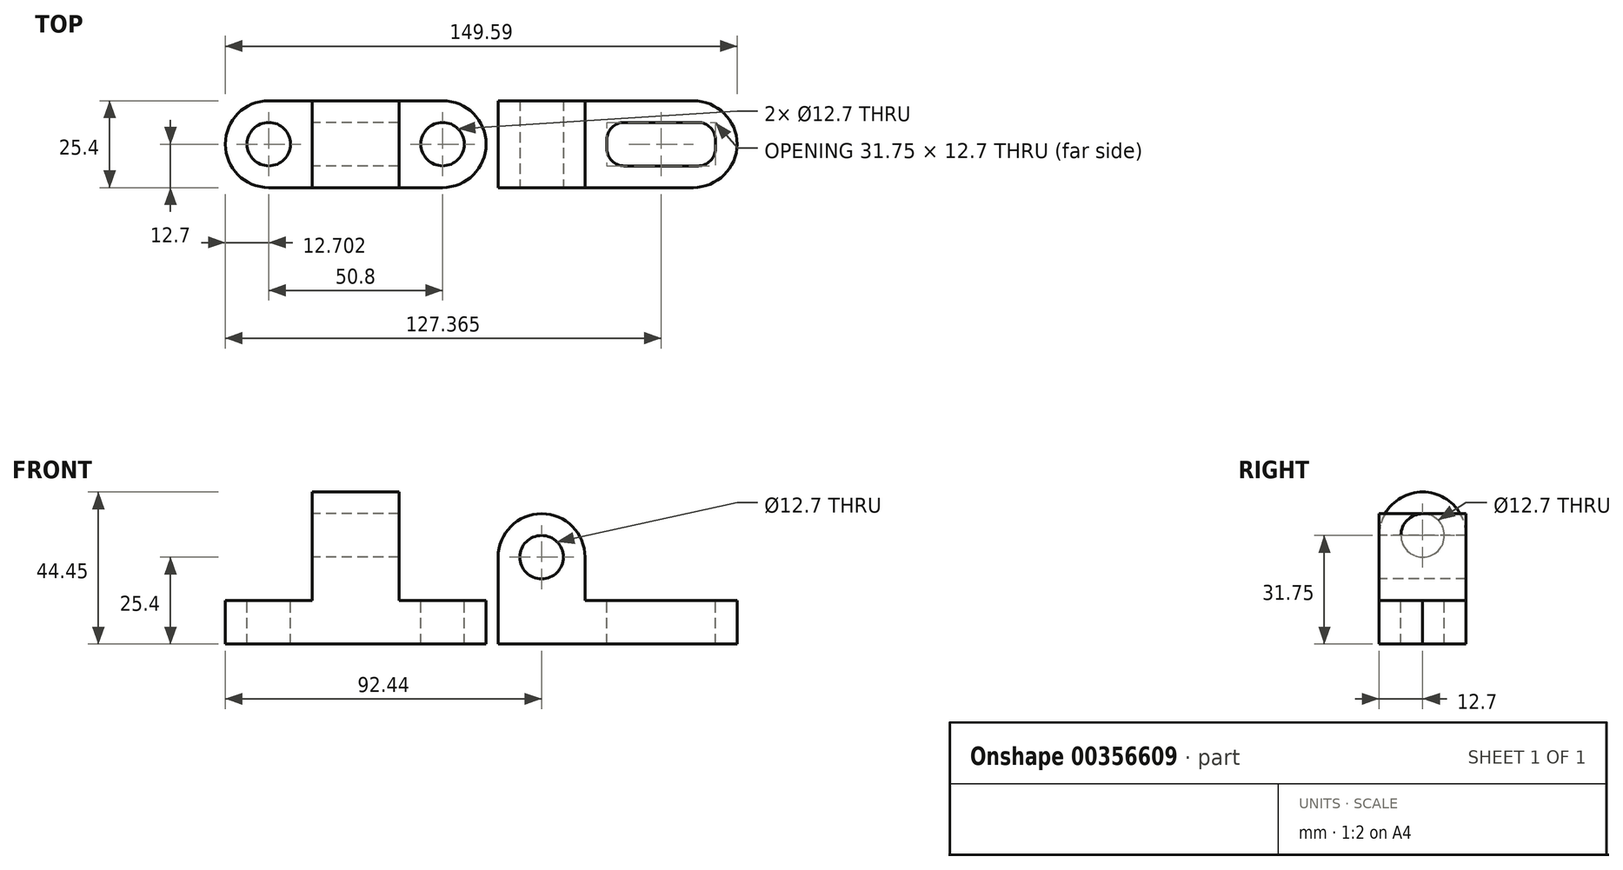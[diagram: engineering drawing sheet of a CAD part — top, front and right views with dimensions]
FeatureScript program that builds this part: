
annotation { "Feature Type Name" : "Feature", "Feature Type Description" : "" }
export const myFeature = defineFeature(function(context is Context, id is Id, definition is map)
    precondition{}
    {
        {
            var Q0;
            Q0=qCreatedBy(makeId("Top.planeOp"),FACE);
            var sketch = newSketch(context, id + "F0", { "sketchPlane" : qUnion([Q0])});
            skLineSegment(sketch, "E0.bottom", {"start": v(0, 0) * mm, "end": v(69.85, 0) * mm});
            skLineSegment(sketch, "E0.top", {"start": v(0, 25.4) * mm, "end": v(69.85, 25.4) * mm});
            skLineSegment(sketch, "E0.left", {"start": v(0, 0) * mm, "end": v(0, 25.4) * mm});
            skLineSegment(sketch, "E0.right", {"start": v(69.85, 0) * mm, "end": v(69.85, 25.4) * mm});
            skSolve(sketch);
        }
        {
            var Q0;
            Q0 = qSketchRegion(id + "F0", true);
            extrude(context, id + "F1", {"entities" : qUnion([Q0]), "depth" : 12.7 * mm});
        }
        {
            var Q0;
            Q0=makeQuery(id+"F1.opExtrude","CAP_FACE",FACE,{"disambiguationData":[OSD([sQuery(id+"F0.wireOp",EDGE,"E0.bottom"),sQuery(id+"F0.wireOp",EDGE,"E0.top"),sQuery(id+"F0.wireOp",EDGE,"E0.left"),sQuery(id+"F0.wireOp",EDGE,"E0.right")])],"isStart":false});
            var sketch = newSketch(context, id + "F2", { "sketchPlane" : qUnion([Q0])});
            skLineSegment(sketch, "E1", {"start": v(25.4, 25.4) * mm, "end": v(25.4, 0) * mm});
            skSolve(sketch);
        }
        {
            var Q0;
            {var subQ0=sQuery(id+"F2.wireOp",EDGE,"E1");Q0=makeQuery(id+"F2.imprint","IMPRINT",FACE,{"disambiguationData":[TD([[makeQuery(id+"F2.imprint","IMPRINT",EDGE,{"derivedFrom":subQ0}),-1.0]])]});}
            extrude(context, id + "F3", {"entities" : qUnion([Q0]), "operationType" : NewBodyOperationType.ADD, "depth" : 25.4 * mm});
        }
        {
            var Q0;
            {var subQ0=sQuery(id+"F0.wireOp",EDGE,"E0.bottom");Q0=makeQuery(id+"F3.boolean.opBoolean","MERGE",FACE,{"derivedFrom":[makeQuery(id+"F1.opExtrude","SWEPT_FACE",FACE,{"disambiguationData":[OSD([subQ0])]}),makeQuery(id+"F3.opExtrude","SWEPT_FACE",FACE,{"disambiguationData":[OSD([subQ0])]})]});}
            var sketch = newSketch(context, id + "F4", { "sketchPlane" : qUnion([Q0])});
            skCircle(sketch, "E2", {"center": v(12.7, 25.4) * mm, "radius": 6.35 * mm});
            skPoint(sketch, "E2.centerSnap0", {"position": v(25.4, 25.4) * mm});
            skPoint(sketch, "E2.centerSnap1", {"position": v(12.7, 38.1) * mm});
            skSolve(sketch);
        }
        {
            var Q0;
            Q0=sQuery(id+"F4.wireOp",VERTEX,"E2.center");
            var Q1;
            Q1=makeQuery(id+"F1.opExtrude","SWEPT_BODY",BODY,{"disambiguationData":[OSD([sQuery(id+"F0.wireOp",EDGE,"E0.bottom"),sQuery(id+"F0.wireOp",EDGE,"E0.top"),sQuery(id+"F0.wireOp",EDGE,"E0.left"),sQuery(id+"F0.wireOp",EDGE,"E0.right")])]});
            hole(context, id + "F5", {"style" : HoleStyle.SIMPLE, "endStyle" : HoleEndStyle.THROUGH, "holeDiameter" : 12.7 * mm, "isTappedThrough" : true, "tappedDepth" : 12.7 * mm, "tapClearance" : 3, "locations" : qUnion([Q0]), "scope" : qUnion([Q1])});
        }
        {
            var Q0;
            Q0=makeQuery(id+"F1.opExtrude","CAP_FACE",FACE,{"disambiguationData":[OSD([sQuery(id+"F0.wireOp",EDGE,"E0.bottom"),sQuery(id+"F0.wireOp",EDGE,"E0.top"),sQuery(id+"F0.wireOp",EDGE,"E0.left"),sQuery(id+"F0.wireOp",EDGE,"E0.right")])],"isStart":false});
            var sketch = newSketch(context, id + "F6", { "sketchPlane" : qUnion([Q0])});
            skLineSegment(sketch, "E3.bottom", {"start": v(31.75, 19.05) * mm, "end": v(63.5, 19.05) * mm});
            skLineSegment(sketch, "E3.top", {"start": v(31.75, 6.35) * mm, "end": v(63.5, 6.35) * mm});
            skLineSegment(sketch, "E3.left", {"start": v(31.75, 19.05) * mm, "end": v(31.75, 6.35) * mm});
            skLineSegment(sketch, "E3.right", {"start": v(63.5, 19.05) * mm, "end": v(63.5, 6.35) * mm});
            skSolve(sketch);
        }
        {
            var Q0;
            Q0 = qSketchRegion(id + "F6", true);
            extrude(context, id + "F7", {"entities" : qUnion([Q0]), "operationType" : NewBodyOperationType.REMOVE, "oppositeDirection" : true, "depth" : 12.7 * mm});
        }
        {
            var Q0;
            {var subQ0=sQuery(id+"F0.wireOp",EDGE,"E0.bottom");Q0=makeQuery(id+"F3.boolean.opBoolean","MERGE",FACE,{"derivedFrom":[makeQuery(id+"F1.opExtrude","SWEPT_FACE",FACE,{"disambiguationData":[OSD([subQ0])]}),makeQuery(id+"F3.opExtrude","SWEPT_FACE",FACE,{"disambiguationData":[OSD([subQ0])]})]});}
            var sketch = newSketch(context, id + "F8", { "sketchPlane" : qUnion([Q0])});
            skCircle(sketch, "E4", {"center": v(12.7, 25.4) * mm, "radius": 12.7 * mm});
            skPoint(sketch, "E4.first.point", {"position": v(12.7, 38.1) * mm});
            skPoint(sketch, "E4.second.point", {"position": v(25.4, 25.4) * mm});
            skPoint(sketch, "E4.third.point", {"position": v(0, 25.4) * mm});
            skPoint(sketch, "E4.third.point.positionSnap0", {"position": v(25.4, 25.4) * mm});
            skSolve(sketch);
        }
        {
            var Q0;
            {var subQ0=sQuery(id+"F8.wireOp",EDGE,"E4");var subQ1=sQuery(id+"F0.wireOp",EDGE,"E0.bottom");var subQ2=makeQuery(id+"F3.opExtrude","CAP_EDGE",EDGE,{"disambiguationData":[OSD([subQ1])],"isStart":false});var subQ3=makeQuery(id+"F8.imprint","INTERSECT",VERTEX,{"derivedFrom":[subQ2,subQ0]});Q0=makeQuery(id+"F8.imprint","IMPRINT",FACE,{"disambiguationData":[TD([[makeQuery(id+"F8.imprint","IMPRINT",EDGE,{"disambiguationData":[TD([[subQ3,-1.0]])],"derivedFrom":subQ0}),-1.0]])]});}
            extrude(context, id + "F9", {"entities" : qUnion([Q0]), "operationType" : NewBodyOperationType.REMOVE, "oppositeDirection" : true, "depth" : 25.4 * mm});
        }
        {
            var Q0;
            {var subQ0=sQuery(id+"F8.wireOp",EDGE,"E4");var subQ1=sQuery(id+"F0.wireOp",EDGE,"E0.bottom");var subQ2=makeQuery(id+"F3.opExtrude","CAP_EDGE",EDGE,{"disambiguationData":[OSD([subQ1])],"isStart":false});var subQ3=makeQuery(id+"F8.imprint","INTERSECT",VERTEX,{"derivedFrom":[subQ2,subQ0]});Q0=makeQuery(id+"F8.imprint","IMPRINT",FACE,{"disambiguationData":[TD([[makeQuery(id+"F8.imprint","IMPRINT",EDGE,{"disambiguationData":[TD([[subQ3,1.0]])],"derivedFrom":subQ0}),-1.0]])]});}
            extrude(context, id + "F10", {"entities" : qUnion([Q0]), "operationType" : NewBodyOperationType.REMOVE, "oppositeDirection" : true, "depth" : 25.4 * mm});
        }
        {
            var Q0;
            Q0=makeQuery(id+"F7.boolean.opBoolean","COPY",EDGE,{"derivedFrom":makeQuery(id+"F7.opExtrude","SWEPT_EDGE",EDGE,{"disambiguationData":[OSD([sQuery(id+"F6.wireOp",EDGE,"E3.bottom"),sQuery(id+"F6.wireOp",EDGE,"E3.left")])]})});
            var Q1;
            Q1=makeQuery(id+"F7.boolean.opBoolean","COPY",EDGE,{"derivedFrom":makeQuery(id+"F7.opExtrude","SWEPT_EDGE",EDGE,{"disambiguationData":[OSD([sQuery(id+"F6.wireOp",EDGE,"E3.top"),sQuery(id+"F6.wireOp",EDGE,"E3.left")])]})});
            var Q2;
            Q2=makeQuery(id+"F7.boolean.opBoolean","COPY",EDGE,{"derivedFrom":makeQuery(id+"F7.opExtrude","SWEPT_EDGE",EDGE,{"disambiguationData":[OSD([sQuery(id+"F6.wireOp",EDGE,"E3.bottom"),sQuery(id+"F6.wireOp",EDGE,"E3.right")])]})});
            var Q3;
            Q3=makeQuery(id+"F7.boolean.opBoolean","COPY",EDGE,{"derivedFrom":makeQuery(id+"F7.opExtrude","SWEPT_EDGE",EDGE,{"disambiguationData":[OSD([sQuery(id+"F6.wireOp",EDGE,"E3.top"),sQuery(id+"F6.wireOp",EDGE,"E3.right")])]})});
            fillet(context, id + "F11", {"entities" : qUnion([Q0, Q1, Q2, Q3]), "radius" : 5.08 * mm, "tangentPropagation" : true, "allowEdgeOverflow" : false});
        }
        {
            var Q0;
            Q0=makeQuery(id+"F1.opExtrude","SWEPT_EDGE",EDGE,{"disambiguationData":[OSD([sQuery(id+"F0.wireOp",EDGE,"E0.top"),sQuery(id+"F0.wireOp",EDGE,"E0.right")])]});
            var Q1;
            Q1=makeQuery(id+"F1.opExtrude","SWEPT_EDGE",EDGE,{"disambiguationData":[OSD([sQuery(id+"F0.wireOp",EDGE,"E0.bottom"),sQuery(id+"F0.wireOp",EDGE,"E0.right")])]});
            fillet(context, id + "F12", {"entities" : qUnion([Q0, Q1]), "radius" : 12.88 * mm, "tangentPropagation" : true, "allowEdgeOverflow" : false});
        }
        {
            var Q0;
            Q0=qCreatedBy(makeId("Top.planeOp"),FACE);
            var sketch = newSketch(context, id + "F13", { "sketchPlane" : qUnion([Q0])});
            skLineSegment(sketch, "E5.bottom", {"start": v(-79.74, 0) * mm, "end": v(-3.54, 0) * mm});
            skLineSegment(sketch, "E5.top", {"start": v(-79.74, 25.4) * mm, "end": v(-3.54, 25.4) * mm});
            skLineSegment(sketch, "E5.left", {"start": v(-79.74, 0) * mm, "end": v(-79.74, 25.4) * mm});
            skLineSegment(sketch, "E5.right", {"start": v(-3.54, 0) * mm, "end": v(-3.54, 25.4) * mm});
            skSolve(sketch);
        }
        {
            var Q0;
            Q0 = qSketchRegion(id + "F13", true);
            extrude(context, id + "F14", {"entities" : qUnion([Q0]), "depth" : 12.7 * mm});
        }
        {
            var Q0;
            Q0=makeQuery(id+"F14.opExtrude","CAP_FACE",FACE,{"disambiguationData":[OSD([sQuery(id+"F13.wireOp",EDGE,"E5.bottom"),sQuery(id+"F13.wireOp",EDGE,"E5.top"),sQuery(id+"F13.wireOp",EDGE,"E5.left"),sQuery(id+"F13.wireOp",EDGE,"E5.right")])],"isStart":false});
            var sketch = newSketch(context, id + "F15", { "sketchPlane" : qUnion([Q0])});
            skLineSegment(sketch, "E6.bottom", {"start": v(-54.34, 25.4) * mm, "end": v(-28.94, 25.4) * mm});
            skLineSegment(sketch, "E6.top", {"start": v(-54.34, 0) * mm, "end": v(-28.94, 0) * mm});
            skLineSegment(sketch, "E6.left", {"start": v(-54.34, 25.4) * mm, "end": v(-54.34, 0) * mm});
            skLineSegment(sketch, "E6.right", {"start": v(-28.94, 25.4) * mm, "end": v(-28.94, 0) * mm});
            skSolve(sketch);
        }
        {
            var Q0;
            Q0=makeQuery(id+"F15.imprint","IMPRINT",FACE,{"disambiguationData":[TD([[makeQuery(id+"F15.imprint","IMPRINT",EDGE,{"derivedFrom":sQuery(id+"F15.wireOp",EDGE,"E6.bottom")}),-1.0]])]});
            extrude(context, id + "F16", {"entities" : qUnion([Q0]), "operationType" : NewBodyOperationType.ADD, "depth" : 31.75 * mm});
        }
        {
            var Q0;
            {var subQ0=sQuery(id+"F13.wireOp",EDGE,"E5.top");var subQ1=sQuery(id+"F13.wireOp",EDGE,"E5.right");var subQ2=sQuery(id+"F13.wireOp",EDGE,"E5.bottom");Q0=makeQuery(id+"F16.boolean.opBoolean","SPLIT",FACE,{"disambiguationData":[TD([makeQuery(id+"F14.opExtrude","SWEPT_FACE",FACE,{"disambiguationData":[OSD([subQ1])]})])],"derivedFrom":makeQuery(id+"F14.opExtrude","CAP_FACE",FACE,{"disambiguationData":[OSD([subQ2,subQ0,sQuery(id+"F13.wireOp",EDGE,"E5.left"),subQ1])],"isStart":false})});}
            var sketch = newSketch(context, id + "F17", { "sketchPlane" : qUnion([Q0])});
            skCircle(sketch, "E7", {"center": v(-16.24, 12.7) * mm, "radius": 6.35 * mm});
            skPoint(sketch, "E7.centerSnap0", {"position": v(-3.54, 12.7) * mm});
            skPoint(sketch, "E7.centerSnap1", {"position": v(-16.24, 25.4) * mm});
            skArc(sketch, "E8", {"start": v(-16.24, 0) * mm, "mid": v(-3.54, 12.7) * mm, "end": v(-16.24, 25.4) * mm});
            skSolve(sketch);
        }
        {
            var Q0;
            Q0 = qSketchRegion(id + "F17", true);
            var Q1;
            {var subQ0=sQuery(id+"F17.wireOp",EDGE,"E8");var subQ1=sQuery(id+"F13.wireOp",EDGE,"E5.right");var subQ5=makeQuery(id+"F14.opExtrude","CAP_EDGE",EDGE,{"disambiguationData":[OSD([subQ1])],"isStart":false});var subQ6=makeQuery(id+"F17.imprint","INTERSECT",VERTEX,{"derivedFrom":[subQ5,subQ0]});Q1=makeQuery(id+"F17.imprint","IMPRINT",FACE,{"disambiguationData":[TD([[makeQuery(id+"F17.imprint","IMPRINT",EDGE,{"disambiguationData":[TD([[subQ6,-1.0]])],"derivedFrom":subQ0}),-1.0]])]});}
            var Q2;
            {var subQ0=sQuery(id+"F17.wireOp",EDGE,"E8");var subQ1=sQuery(id+"F13.wireOp",EDGE,"E5.right");var subQ5=makeQuery(id+"F14.opExtrude","CAP_EDGE",EDGE,{"disambiguationData":[OSD([subQ1])],"isStart":false});var subQ6=makeQuery(id+"F17.imprint","INTERSECT",VERTEX,{"derivedFrom":[subQ5,subQ0]});Q2=makeQuery(id+"F17.imprint","IMPRINT",FACE,{"disambiguationData":[TD([[makeQuery(id+"F17.imprint","IMPRINT",EDGE,{"disambiguationData":[TD([[subQ6,1.0]])],"derivedFrom":subQ0}),-1.0]])]});}
            extrude(context, id + "F18", {"entities" : qUnion([Q0, Q1, Q2]), "operationType" : NewBodyOperationType.REMOVE, "oppositeDirection" : true, "depth" : 12.7 * mm});
        }
        {
            var Q0;
            {var subQ0=sQuery(id+"F13.wireOp",EDGE,"E5.left");var subQ1=sQuery(id+"F13.wireOp",EDGE,"E5.top");var subQ2=sQuery(id+"F13.wireOp",EDGE,"E5.bottom");Q0=makeQuery(id+"F16.boolean.opBoolean","SPLIT",FACE,{"disambiguationData":[TD([makeQuery(id+"F14.opExtrude","SWEPT_FACE",FACE,{"disambiguationData":[OSD([subQ0])]})])],"derivedFrom":makeQuery(id+"F14.opExtrude","CAP_FACE",FACE,{"disambiguationData":[OSD([subQ2,subQ1,subQ0,sQuery(id+"F13.wireOp",EDGE,"E5.right")])],"isStart":false})});}
            var sketch = newSketch(context, id + "F19", { "sketchPlane" : qUnion([Q0])});
            skCircle(sketch, "E9", {"center": v(-67.04, 12.7) * mm, "radius": 6.35 * mm});
            skPoint(sketch, "E9.centerSnap0", {"position": v(-79.74, 12.7) * mm});
            skPoint(sketch, "E9.centerSnap1", {"position": v(-67.04, 25.4) * mm});
            skArc(sketch, "E10", {"start": v(-67.04, 25.4) * mm, "mid": v(-79.74, 12.7) * mm, "end": v(-67.04, 0) * mm});
            skSolve(sketch);
        }
        {
            var Q0;
            Q0 = qSketchRegion(id + "F19", true);
            var Q1;
            {var subQ0=sQuery(id+"F19.wireOp",EDGE,"E10");var subQ1=sQuery(id+"F13.wireOp",EDGE,"E5.left");var subQ5=makeQuery(id+"F14.opExtrude","CAP_EDGE",EDGE,{"disambiguationData":[OSD([subQ1])],"isStart":false});var subQ6=makeQuery(id+"F19.imprint","INTERSECT",VERTEX,{"derivedFrom":[subQ5,subQ0]});Q1=makeQuery(id+"F19.imprint","IMPRINT",FACE,{"disambiguationData":[TD([[makeQuery(id+"F19.imprint","IMPRINT",EDGE,{"disambiguationData":[TD([[subQ6,1.0]])],"derivedFrom":subQ0}),-1.0]])]});}
            var Q2;
            {var subQ0=sQuery(id+"F19.wireOp",EDGE,"E10");var subQ1=sQuery(id+"F13.wireOp",EDGE,"E5.left");var subQ5=makeQuery(id+"F14.opExtrude","CAP_EDGE",EDGE,{"disambiguationData":[OSD([subQ1])],"isStart":false});var subQ6=makeQuery(id+"F19.imprint","INTERSECT",VERTEX,{"derivedFrom":[subQ5,subQ0]});Q2=makeQuery(id+"F19.imprint","IMPRINT",FACE,{"disambiguationData":[TD([[makeQuery(id+"F19.imprint","IMPRINT",EDGE,{"disambiguationData":[TD([[subQ6,-1.0]])],"derivedFrom":subQ0}),-1.0]])]});}
            extrude(context, id + "F20", {"entities" : qUnion([Q0, Q1, Q2]), "operationType" : NewBodyOperationType.REMOVE, "oppositeDirection" : true, "depth" : 12.7 * mm});
        }
        {
            var Q0;
            Q0=makeQuery(id+"F16.opExtrude","SWEPT_FACE",FACE,{"disambiguationData":[OSD([sQuery(id+"F15.wireOp",EDGE,"E6.left")])]});
            var sketch = newSketch(context, id + "F21", { "sketchPlane" : qUnion([Q0])});
            skPoint(sketch, "E11.centerSnap0", {"position": v(-12.7, 44.45) * mm});
            skPoint(sketch, "E11.centerSnap1", {"position": v(0, 34.93) * mm});
            skCircle(sketch, "E12", {"center": v(-12.7, 31.75) * mm, "radius": 6.35 * mm});
            skArc(sketch, "E13", {"start": v(0, 31.75) * mm, "mid": v(-12.7, 44.45) * mm, "end": v(-25.4, 31.75) * mm});
            skSolve(sketch);
        }
        {
            var Q0;
            Q0 = qSketchRegion(id + "F21", true);
            var Q1;
            {var subQ0=sQuery(id+"F21.wireOp",EDGE,"E13");var subQ1=sQuery(id+"F15.wireOp",EDGE,"E6.left");var subQ4=makeQuery(id+"F16.opExtrude","CAP_EDGE",EDGE,{"disambiguationData":[OSD([subQ1])],"isStart":false});var subQ5=makeQuery(id+"F21.imprint","INTERSECT",VERTEX,{"derivedFrom":[subQ4,subQ0]});Q1=makeQuery(id+"F21.imprint","IMPRINT",FACE,{"disambiguationData":[TD([[makeQuery(id+"F21.imprint","IMPRINT",EDGE,{"disambiguationData":[TD([[subQ5,-1.0]])],"derivedFrom":subQ0}),-1.0]])]});}
            var Q2;
            {var subQ0=sQuery(id+"F21.wireOp",EDGE,"E13");var subQ1=sQuery(id+"F15.wireOp",EDGE,"E6.left");var subQ4=makeQuery(id+"F16.opExtrude","CAP_EDGE",EDGE,{"disambiguationData":[OSD([subQ1])],"isStart":false});var subQ5=makeQuery(id+"F21.imprint","INTERSECT",VERTEX,{"derivedFrom":[subQ4,subQ0]});Q2=makeQuery(id+"F21.imprint","IMPRINT",FACE,{"disambiguationData":[TD([[makeQuery(id+"F21.imprint","IMPRINT",EDGE,{"disambiguationData":[TD([[subQ5,1.0]])],"derivedFrom":subQ0}),-1.0]])]});}
            extrude(context, id + "F22", {"entities" : qUnion([Q0, Q1, Q2]), "operationType" : NewBodyOperationType.REMOVE, "oppositeDirection" : true, "depth" : 25.4 * mm});
        }
    });
